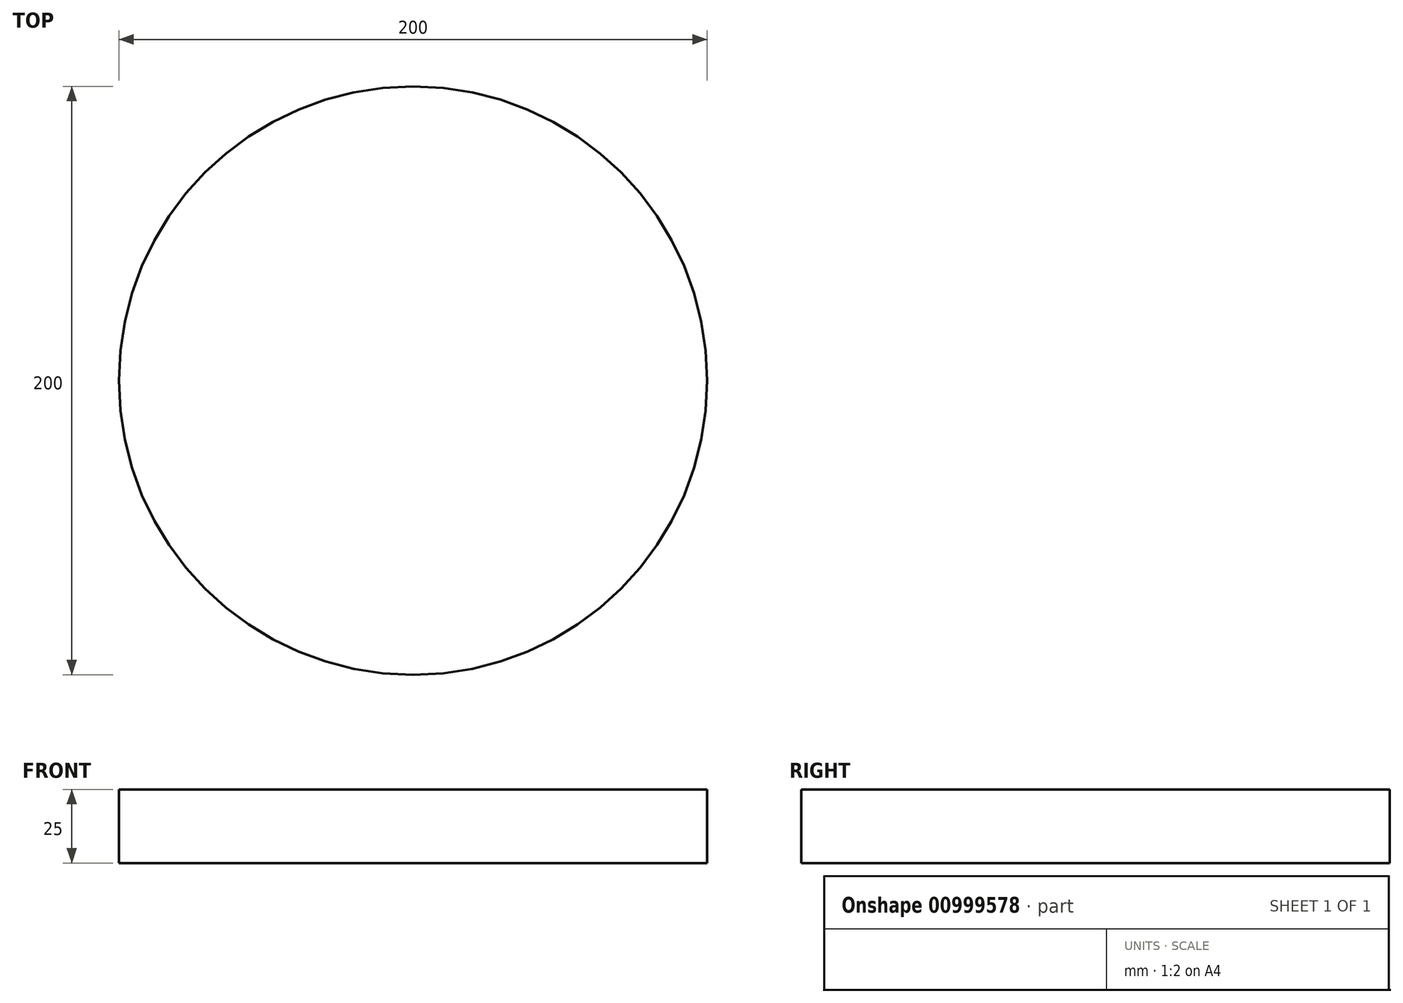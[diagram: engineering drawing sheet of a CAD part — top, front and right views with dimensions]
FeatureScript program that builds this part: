
annotation { "Feature Type Name" : "Feature", "Feature Type Description" : "" }
export const myFeature = defineFeature(function(context is Context, id is Id, definition is map)
    precondition{}
    {
        {
            var Q0;
            Q0=qCreatedBy(makeId("Top.planeOp"),FACE);
            var sketch = newSketch(context, id + "F0", { "sketchPlane" : qUnion([Q0])});
            skCircle(sketch, "E0", {"center": v(0, 0) * mm, "radius": 100 * mm});
            skSolve(sketch);
        }
        {
            var Q0;
            Q0 = qSketchRegion(id + "F0", true);
            extrude(context, id + "F1", {"entities" : qUnion([Q0]), "depth" : 25 * mm, "offsetDistance" : 25 * mm});
        }
    });
